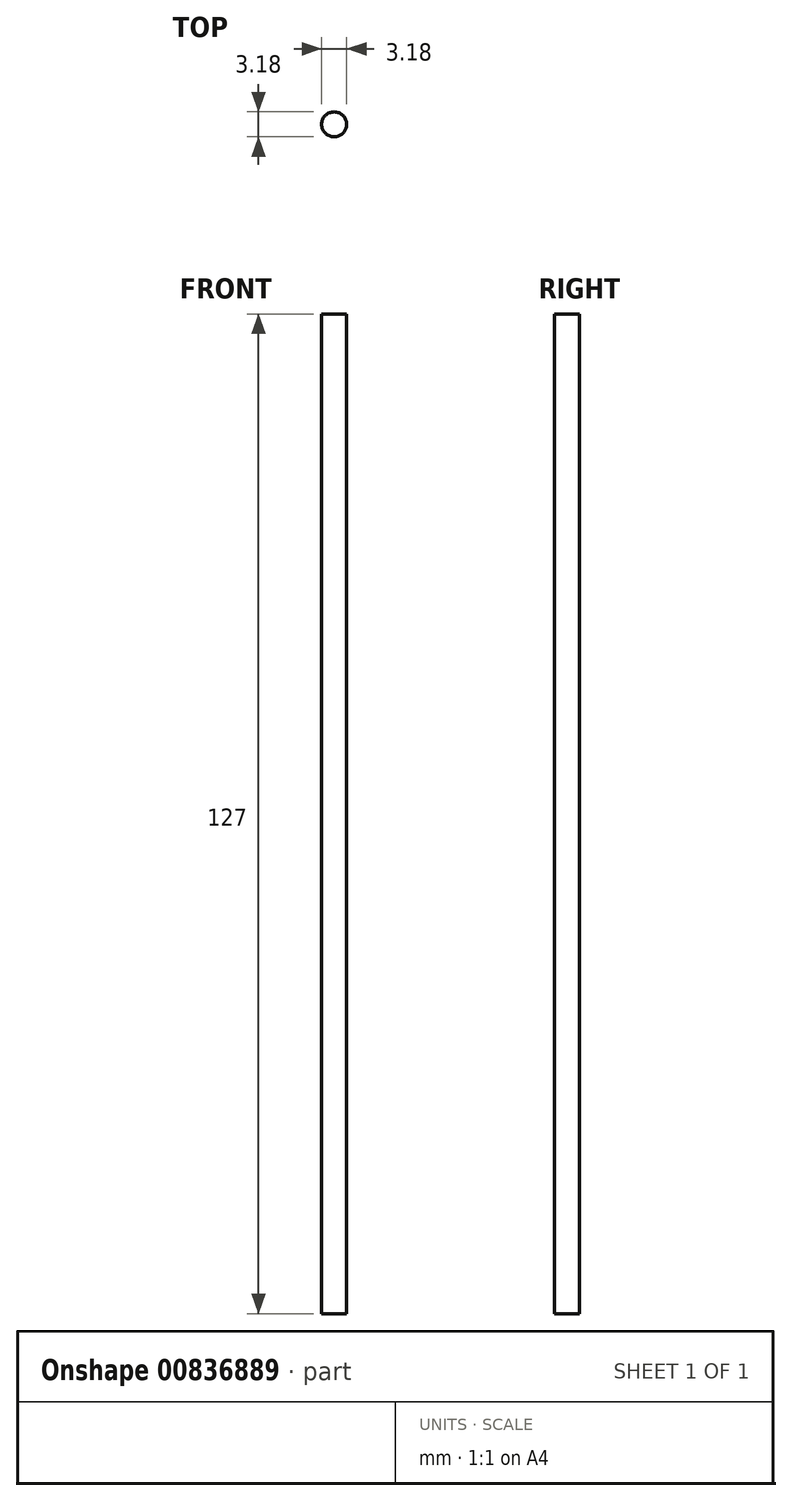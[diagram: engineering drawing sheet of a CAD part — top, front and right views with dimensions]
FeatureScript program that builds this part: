
annotation { "Feature Type Name" : "Feature", "Feature Type Description" : "" }
export const myFeature = defineFeature(function(context is Context, id is Id, definition is map)
    precondition{}
    {
        {
            var Q0;
            Q0=qCreatedBy(makeId("Top.planeOp"),FACE);
            var sketch = newSketch(context, id + "F0", { "sketchPlane" : qUnion([Q0])});
            skCircle(sketch, "E0", {"center": v(0, 0) * mm, "radius": 1.59 * mm});
            skSolve(sketch);
        }
        {
            var Q0;
            Q0 = qSketchRegion(id + "F0", true);
            extrude(context, id + "F1", {"entities" : qUnion([Q0]), "depth" : 127 * mm, "offsetDistance" : 25.4 * mm});
        }
    });
